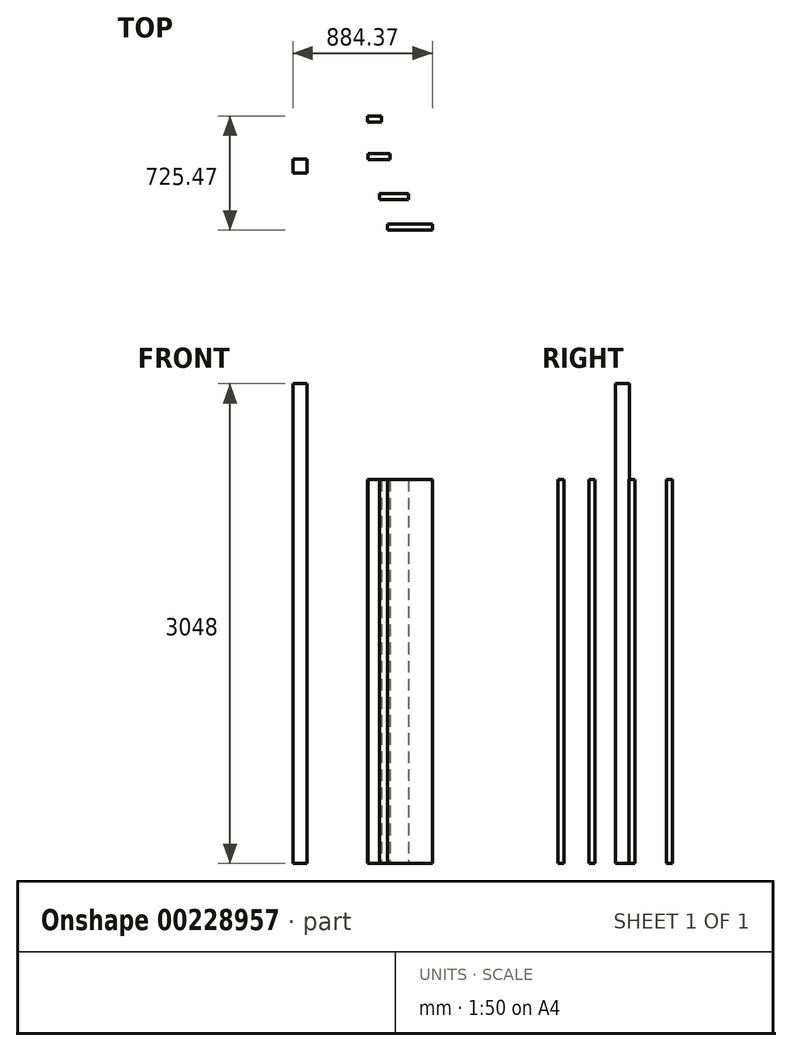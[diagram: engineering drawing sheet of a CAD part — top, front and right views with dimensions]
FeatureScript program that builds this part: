
annotation { "Feature Type Name" : "Feature", "Feature Type Description" : "" }
export const myFeature = defineFeature(function(context is Context, id is Id, definition is map)
    precondition{}
    {
        {
            var Q0;
            Q0=qCreatedBy(makeId("Top.planeOp"),FACE);
            var sketch = newSketch(context, id + "F0", { "sketchPlane" : qUnion([Q0])});
            skLineSegment(sketch, "E0.bottom", {"start": v(-177.39, 113.37) * mm, "end": v(-88.49, 113.37) * mm});
            skLineSegment(sketch, "E0.top", {"start": v(-177.39, 24.47) * mm, "end": v(-88.49, 24.47) * mm});
            skLineSegment(sketch, "E0.left", {"start": v(-177.39, 113.37) * mm, "end": v(-177.39, 24.47) * mm});
            skLineSegment(sketch, "E0.right", {"start": v(-88.49, 113.37) * mm, "end": v(-88.49, 24.47) * mm});
            skSolve(sketch);
        }
        {
            var Q0;
            Q0=qSketchRegion(id+"F0",true);
            extrude(context, id + "F1", {"entities" : qUnion([Q0]), "depth" : 3048 * mm});
        }
        {
            var Q0;
            Q0=qCreatedBy(makeId("Top.planeOp"),FACE);
            var sketch = newSketch(context, id + "F2", { "sketchPlane" : qUnion([Q0])});
            skLineSegment(sketch, "E1.bottom", {"start": v(296.02, 385.67) * mm, "end": v(384.92, 385.67) * mm});
            skLineSegment(sketch, "E1.top", {"start": v(296.02, 347.57) * mm, "end": v(384.92, 347.57) * mm});
            skLineSegment(sketch, "E1.left", {"start": v(296.02, 385.67) * mm, "end": v(296.02, 347.57) * mm});
            skLineSegment(sketch, "E1.right", {"start": v(384.92, 385.67) * mm, "end": v(384.92, 347.57) * mm});
            skSolve(sketch);
        }
        {
            var Q0;
            Q0=qSketchRegion(id+"F2",true);
            extrude(context, id + "F3", {"entities" : qUnion([Q0]), "depth" : 2438.4 * mm});
        }
        {
            var Q0;
            Q0=qCreatedBy(makeId("Top.planeOp"),FACE);
            var sketch = newSketch(context, id + "F4", { "sketchPlane" : qUnion([Q0])});
            skLineSegment(sketch, "E2.bottom", {"start": v(300.13, 147.9) * mm, "end": v(439.83, 147.9) * mm});
            skLineSegment(sketch, "E2.top", {"start": v(300.13, 109.8) * mm, "end": v(439.83, 109.8) * mm});
            skLineSegment(sketch, "E2.left", {"start": v(300.13, 147.9) * mm, "end": v(300.13, 109.8) * mm});
            skLineSegment(sketch, "E2.right", {"start": v(439.83, 147.9) * mm, "end": v(439.83, 109.8) * mm});
            skSolve(sketch);
        }
        {
            var Q0;
            Q0=makeQuery(id+"F4.imprint","IMPRINT",FACE,{"disambiguationData":[TD([[makeQuery(id+"F4.imprint","IMPRINT",EDGE,{"derivedFrom":sQuery(id+"F4.wireOp",EDGE,"E2.bottom")}),-1.0]])]});
            extrude(context, id + "F5", {"entities" : qUnion([Q0]), "depth" : 2438.4 * mm});
        }
        {
            var Q0;
            Q0=qCreatedBy(makeId("Top.planeOp"),FACE);
            var sketch = newSketch(context, id + "F6", { "sketchPlane" : qUnion([Q0])});
            skLineSegment(sketch, "E3.bottom", {"start": v(371.97, -106.57) * mm, "end": v(556.12, -106.57) * mm});
            skLineSegment(sketch, "E3.top", {"start": v(371.97, -144.67) * mm, "end": v(556.12, -144.67) * mm});
            skLineSegment(sketch, "E3.left", {"start": v(371.97, -106.57) * mm, "end": v(371.97, -144.67) * mm});
            skLineSegment(sketch, "E3.right", {"start": v(556.12, -106.57) * mm, "end": v(556.12, -144.67) * mm});
            skSolve(sketch);
        }
        {
            var Q0;
            Q0=makeQuery(id+"F6.imprint","IMPRINT",FACE,{"disambiguationData":[TD([[makeQuery(id+"F6.imprint","IMPRINT",EDGE,{"derivedFrom":sQuery(id+"F6.wireOp",EDGE,"E3.bottom")}),-1.0]])]});
            extrude(context, id + "F7", {"entities" : qUnion([Q0]), "depth" : 2438.4 * mm});
        }
        {
            var Q0;
            Q0=qCreatedBy(makeId("Top.planeOp"),FACE);
            var sketch = newSketch(context, id + "F8", { "sketchPlane" : qUnion([Q0])});
            skLineSegment(sketch, "E4.bottom", {"start": v(421.23, -301.7) * mm, "end": v(706.98, -301.7) * mm});
            skLineSegment(sketch, "E4.top", {"start": v(421.23, -339.8) * mm, "end": v(706.98, -339.8) * mm});
            skLineSegment(sketch, "E4.left", {"start": v(421.23, -301.7) * mm, "end": v(421.23, -339.8) * mm});
            skLineSegment(sketch, "E4.right", {"start": v(706.98, -301.7) * mm, "end": v(706.98, -339.8) * mm});
            skSolve(sketch);
        }
        {
            var Q0;
            Q0=makeQuery(id+"F8.imprint","IMPRINT",FACE,{"disambiguationData":[TD([[makeQuery(id+"F8.imprint","IMPRINT",EDGE,{"derivedFrom":sQuery(id+"F8.wireOp",EDGE,"E4.bottom")}),-1.0]])]});
            extrude(context, id + "F9", {"entities" : qUnion([Q0]), "depth" : 2438.4 * mm});
        }
    });
